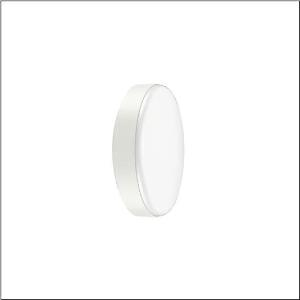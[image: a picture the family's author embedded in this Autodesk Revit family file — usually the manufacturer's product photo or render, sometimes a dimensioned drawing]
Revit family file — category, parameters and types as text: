
# Revit family: rondel_31_51wc10da32a
name_source: partatom
category: Lighting Fixtures
units: mm (PartAtom-declared; Revit-internal decimal feet)

## family parameters
Cut with Voids When Loaded = No
Host = Face
Light Source = No
Part Type = Normal
Room Calculation Point = No
Round Connector Dimension = Use Diameter
Shared = No

## types (1)
- Rondel 31 (1 x LED, 2450 lm, 19 W, 3000K)
    Apparent Load = 19 VA
    CIE Flux Codes = 44 75 94 94 100
    Color Rendering = 80
    Color Temperature = 3000K
    Default Elevation = 1800 mm
    Description = Rondel 31, wall and ceiling luminaire, primary optical cover: cover, of PC, opal, light emission: direct distribution, primary light characteristic: symmetric, installation type: surface-mounted, LED, rated luminous flux: 2.450lm, luminous efficacy: 129lm/W, light colour: 830, colour temperature: 3000K, with terminal, 5-pole, max. 2.5mm², mains connection: 220..240V, AC, 50/60Hz, rated input power: 19W, luminaire housing, of PC, traffic white (RAL 9016), diameter: 350mm, protection rating (complete): IP65, insulation class (complete): insulation class II (safety insulation), certification: CE, impact resistance: IK10, permissible operating ambient temperature: -20..+40°C, permissible storage temperature: -20..+60°C, packaging unit: 1 piece
    Height = 97 mm
    Lamp = 1 x LED
    Lamp Light Flux = 2450 lm
    Lamp Power = 19 W
    Lamp count = 1
    Length = 350 mm
    Luminous efficacy = 129 lm/W
    Manufacturer = Siteco
    ModVariant = No
    Model = 51WC10DA32A
    Mounting Place = Ceiling
    Mounting Type = Surface mounted
    Number of Poles = 1
    OnlyDefault = Yes
    Power Factor = 1
    Product Name = Rondel 31
    Product group = wall and ceiling luminaire
    ProductGroupID = 302
    Protection Class = Protection class II
    Protection Degree = IP 65
    RLX_Detail_Level = 1
    RLX_Emergency_Light_Flux = 0 lm
    RLX_Emergency_Type = 0
    RLX_Emergency_Type_DB = No
    RlxData = <blob elided: 29649 chars, md5=d0f24c1d>
    Socket = socket
    Standby Power = 0 W
    System Light Flux = 2450 lm
    System Power = 19 W
    Type Comments = Product without accessories
    Type Image = l_1007027.jpg
    URL = http://relux.com
    VarID = ---
    Voltage = 0 V
    Weight = 0.00 kg
    Width = 0 mm  [stored 0 ft]

note: [stored X ft] marks values corroborated as IEEE doubles in the binary element streams (Revit-internal decimal feet)

## geometry (parser evidence)
native form markers: Blend x4, Sweep x12
no freeform markers — native parametric forms only
